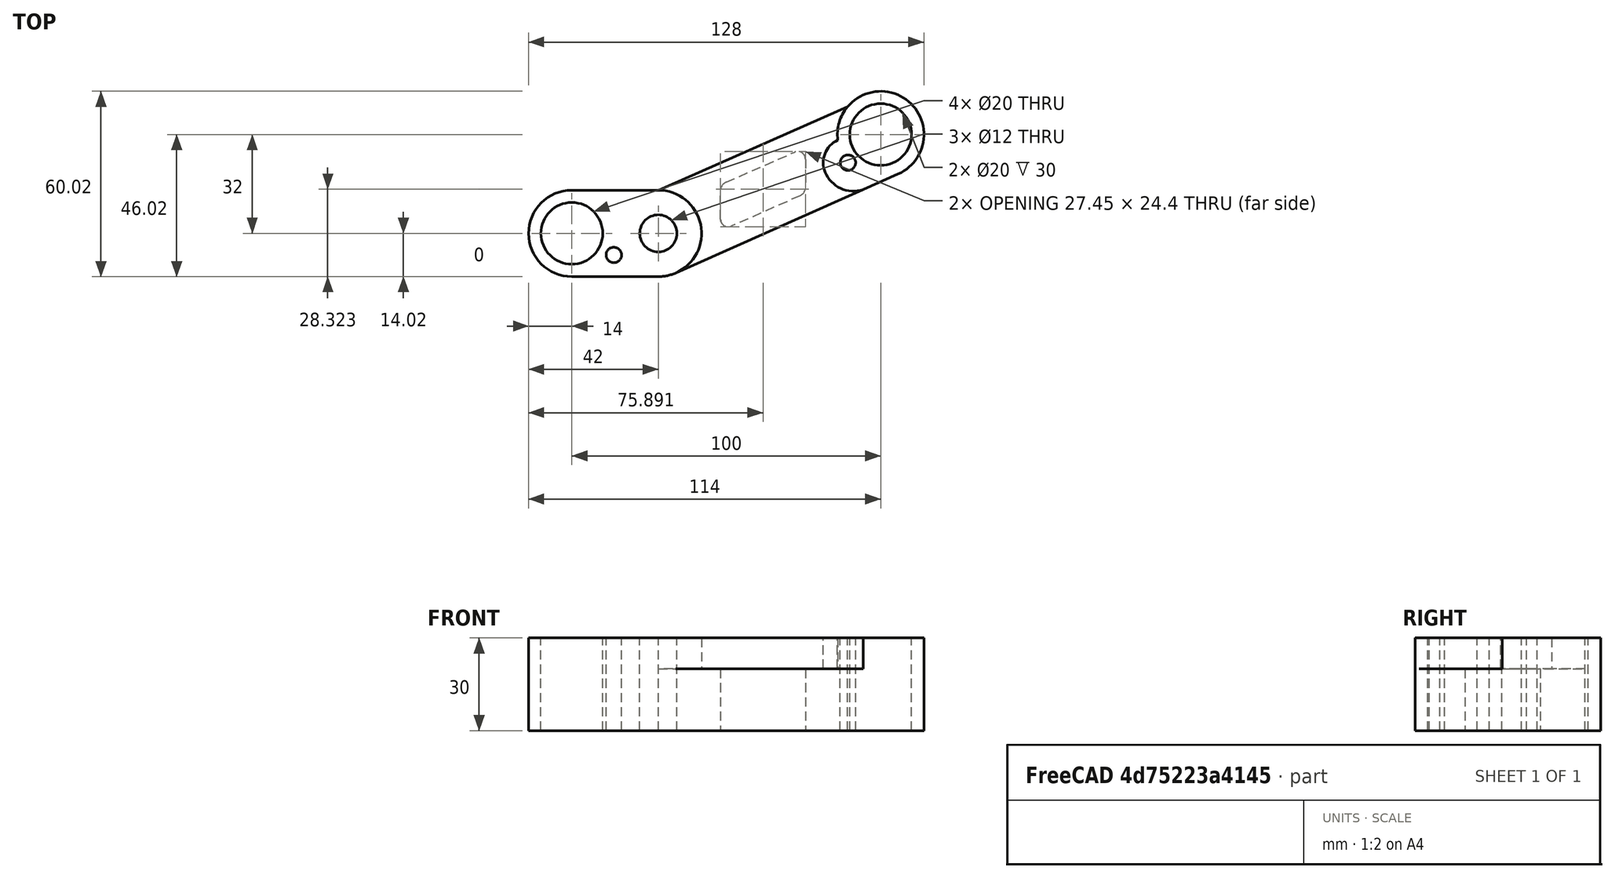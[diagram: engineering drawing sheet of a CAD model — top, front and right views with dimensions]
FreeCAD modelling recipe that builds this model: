
FCSTD DOCUMENT  (FreeCAD 0.15R4630 (Git))
Label: x_carriage_center
License: All rights reserved
LicenseURL: http://en.wikipedia.org/wiki/All_rights_reserved
objects: Part::Cylinder×5, Part::Cut×4, Sketcher::SketchObject×3, Part::MultiFuse×2, Part::Feature×2, Part::Extrusion×2, Part::Fillet×2, Mesh::Feature×1, PartDesign::Pocket×1
note: 22 computed .brp shape members not serialized (recipe doc carries the construction recipe); baked Part::Feature solids carry a one-line shape summary decoded from their .brp

FEATURE [Part::Cylinder] Cylinder002  label="Cilindro001"
  Angle = 360
  Height = 32
  Placement = pos=(14,14,-1) rot=(0,0,1;0rad)
  Radius = 10
FEATURE [Part::Cylinder] Cylinder003  label="Cilindro002"
  Angle = 360
  Height = 32
  Placement = pos=(114,46,-1) rot=(0,0,1;0rad)
  Radius = 10
FEATURE [Part::Cylinder] Cylinder004  label="threaded_rod_hole"
  Angle = 360
  Height = 32
  Placement = pos=(42,14,-1) rot=(0,0,1;0rad)
  Radius = 6
FEATURE [Part::MultiFuse] Fusion003  label="bearing_holes"
  Shapes = -> [Cylinder002,Cylinder003]
FEATURE [Part::Cylinder] Cylinder007  label="Cilindro005"
  Angle = 360
  Height = 32
  Placement = pos=(27.6,7,-1) rot=(0,0,1;0rad)
  Radius = 2.5
FEATURE [Part::Cylinder] Cylinder008  label="Cilindro006"
  Angle = 360
  Height = 32
  Placement = pos=(103.4,36.9,-1) rot=(0,0,1;0rad)
  Radius = 2.5
FEATURE [Part::MultiFuse] Fusion007  label="joined_holes"
  Shapes = -> [Cylinder008,Cylinder007]
FEATURE [Mesh::Feature] Xcariagecenter
  Placement = pos=(128,60,0) rot=(0,0,1;3.14159rad)
FEATURE [Part::Feature] Xcariagecenter001001  label="Xcariagecenter002"
  shape: bbox 128 x 60.02 x 30 mm, 1617 faces, 0 solids (baked)
FEATURE [Sketcher::SketchObject] Sketch
  ExternalGeometry = -> [Xcariagecenter001001]
  Placement = pos=(0,0,2.86102e-06) rot=(0,0,1;0rad)
  Support = -> Xcariagecenter001001 [Face1611]
  sketch-geometry (8):
    g0: LineSegment StartX=42.0005 StartY=27.9846 StartZ=0 EndX=14.0005 EndY=27.9846 EndZ=0
    g1: ArcOfCircle CenterX=14.0005 CenterY=13.9846 CenterZ=0 NormalX=0 NormalY=0 NormalZ=1 Radius=14 StartAngle=1.5708 EndAngle=4.71239
    g2: ArcOfCircle CenterX=114 CenterY=46.0002 CenterZ=0 NormalX=0 NormalY=0 NormalZ=1 Radius=14 StartAngle=5.13079 EndAngle=8.72942
    g3: ArcOfCircle CenterX=42.0005 CenterY=13.9846 CenterZ=0 NormalX=0 NormalY=0 NormalZ=1 Radius=14 StartAngle=4.71239 EndAngle=5.1308
    g4: LineSegment StartX=108.323 StartY=28.1541 StartZ=0 EndX=119.689 EndY=33.2079 EndZ=0
    g5: LineSegment StartX=108.323 StartY=28.1541 StartZ=0 EndX=47.6888 EndY=1.19228 EndZ=0
    g6: LineSegment StartX=103.251 StartY=54.9695 StartZ=0 EndX=42.0005 EndY=27.9846 EndZ=0
    g7: LineSegment StartX=14.0005 StartY=-0.0153961 StartZ=0 EndX=42.0005 EndY=-0.0153961 EndZ=0
  constraints (19):
    c: Coincident(g0,g-7)
    c: Coincident(g0,g-9)
    c: Coincident(g1,g0)
    c: PointOnObject(g-10,g1)
    c: PointOnObject(g-4,g2)
    c: Coincident(g4,g-11)
    c: Coincident(g4,g2)
    c: Coincident(g5,g4)
    c: Coincident(g5,g3)
    c: Coincident(g2,g-5)
    c: Coincident(g3,g-8)
    c: Coincident(g0,g6)
    c: Coincident(g2,g6)
    c: Coincident(g2,g-12)
    c: Coincident(g1,g-13)
    c: Coincident(g3,g-14)
    c: Radius(g3) = 14
    c: Coincident(g7,g1)
    c: Coincident(g7,g3)
FEATURE [Part::Extrusion] Extrude
  Base = -> Sketch
  Dir = (0,0,30)
  Solid = true
FEATURE [Part::Cut] Cut
  Base = -> Extrude
  Tool = -> Fusion003
FEATURE [Part::Cut] Cut001
  Base = -> Cut
  Tool = -> Cylinder004
FEATURE [Part::Cut] Cut002
  Base = -> Cut001
  Tool = -> Fusion007
FEATURE [Sketcher::SketchObject] Sketch001
  ExternalGeometry = -> [Cut002]
  Placement = pos=(0,0,30) rot=(0,0,1;0rad)
  Support = -> Cut002 [Face5]
  sketch-geometry (6):
    g0: ArcOfCircle CenterX=114 CenterY=46 CenterZ=0 NormalX=0 NormalY=0 NormalZ=1 Radius=13.9998 StartAngle=2.4462 EndAngle=3.27086
    g1: ArcOfCircle CenterX=103.4 CenterY=36.9 CenterZ=0 NormalX=0 NormalY=0 NormalZ=1 Radius=8 StartAngle=1.99366 EndAngle=3.53622
    g2: ArcOfCircle CenterX=105.246 CenterY=37.6689 CenterZ=0 NormalX=0 NormalY=0 NormalZ=1 Radius=10 StartAngle=3.53622 EndAngle=5.02515
    g3: LineSegment StartX=42.0005 StartY=27.9846 StartZ=0 EndX=103.251 EndY=54.9695 EndZ=0
    g4: LineSegment StartX=108.323 StartY=28.1541 StartZ=0 EndX=47.6888 EndY=1.19228 EndZ=0
    g5: ArcOfCircle CenterX=42.0005 CenterY=13.9846 CenterZ=0 NormalX=0 NormalY=0 NormalZ=1 Radius=14 StartAngle=5.1308 EndAngle=7.85398
  constraints (16):
    c: Coincident(g0,g-5)
    c: Coincident(g1,g-3)
    c: Coincident(g1,g0)
    c: Coincident(g2,g1)
    c: Coincident(g2,g-4)
    c: Tangent(g2,g1)
    c: Radius(g1) = 8
    c: Radius(g2) = 10
    c: Coincident(g0,g-6)
    c: Coincident(g3,g0)
    c: Coincident(g4,g2)
    c: Coincident(g5,g3)
    c: Coincident(g5,g4)
    c: Coincident(g4,g-4)
    c: Coincident(g3,g-5)
    c: Radius(g5) = 14
FEATURE [PartDesign::Pocket] Pocket  label="x_carriage_center"
  Length = 10
  Sketch = -> Sketch001
  Type = 0
FEATURE [Sketcher::SketchObject] Sketch002
  ExternalGeometry = -> [Pocket]
  Placement = pos=(0,0,20) rot=(0,0,1;0rad)
  Support = -> Pocket [Face8]
  sketch-geometry (7):
    g0: LineSegment StartX=62.1646 StartY=29.7487 StartZ=0 EndX=89.6183 EndY=41.8438 EndZ=0
    g1: LineSegment StartX=89.6183 StartY=41.8438 StartZ=0 EndX=89.6183 EndY=26.9563 EndZ=0
    g2: LineSegment StartX=89.6183 StartY=26.9563 StartZ=0 EndX=62.1646 EndY=14.7487 EndZ=0
    g3: LineSegment StartX=62.1646 StartY=14.7487 StartZ=0 EndX=62.1646 EndY=29.7487 EndZ=0
    g4: LineSegment [constr] StartX=89.6183 StartY=26.9563 StartZ=0 EndX=89.6183 EndY=19.8367 EndZ=0
    g5: LineSegment [constr] StartX=89.6183 StartY=41.8438 StartZ=0 EndX=89.6183 EndY=48.9634 EndZ=0
    g6: LineSegment [constr] StartX=62.1646 StartY=29.7487 StartZ=0 EndX=46.0046 EndY=29.7487 EndZ=0
  constraints (21):
    c: Coincident(g0,g1)
    c: Coincident(g1,g2)
    c: Coincident(g2,g3)
    c: Coincident(g3,g0)
    c: Vertical(g1)
    c: Vertical(g3)
    c: Parallel(g0,g-4)
    c: Parallel(g2,g-3)
    c: Distance(g0) = 30
    c: DistanceY(g3) = 15
    c: Coincident(g4,g1)
    c: PointOnObject(g4,g-3)
    c: Vertical(g4)
    c: Coincident(g5,g0)
    c: PointOnObject(g5,g-4)
    c: Vertical(g5)
    c: Equal(g4,g5)
    c: Coincident(g6,g0)
    c: PointOnObject(g6,g-4)
    c: Horizontal(g6)
    c: DistanceX(g6) = -16.16
FEATURE [Part::Extrusion] Extrude002
  Base = -> Sketch002
  Dir = (0,0,-20)
  Solid = true
FEATURE [Part::Cut] Cut003
  Base = -> Pocket
  Tool = -> Extrude002
FEATURE [Part::Fillet] Fillet
  Base = -> Cut003
  Edges = 2 edges r=3: [Edge59,Edge61]
FEATURE [Part::Fillet] Fillet001
  Base = -> Fillet
  Edges = 2 edges r=2.5: [Edge22,Edge28]
FEATURE [Part::Feature] Fillet001001  label="Fillet002"
  shape: bbox 128 x 60.02 x 30 mm, 28 faces (baked)
